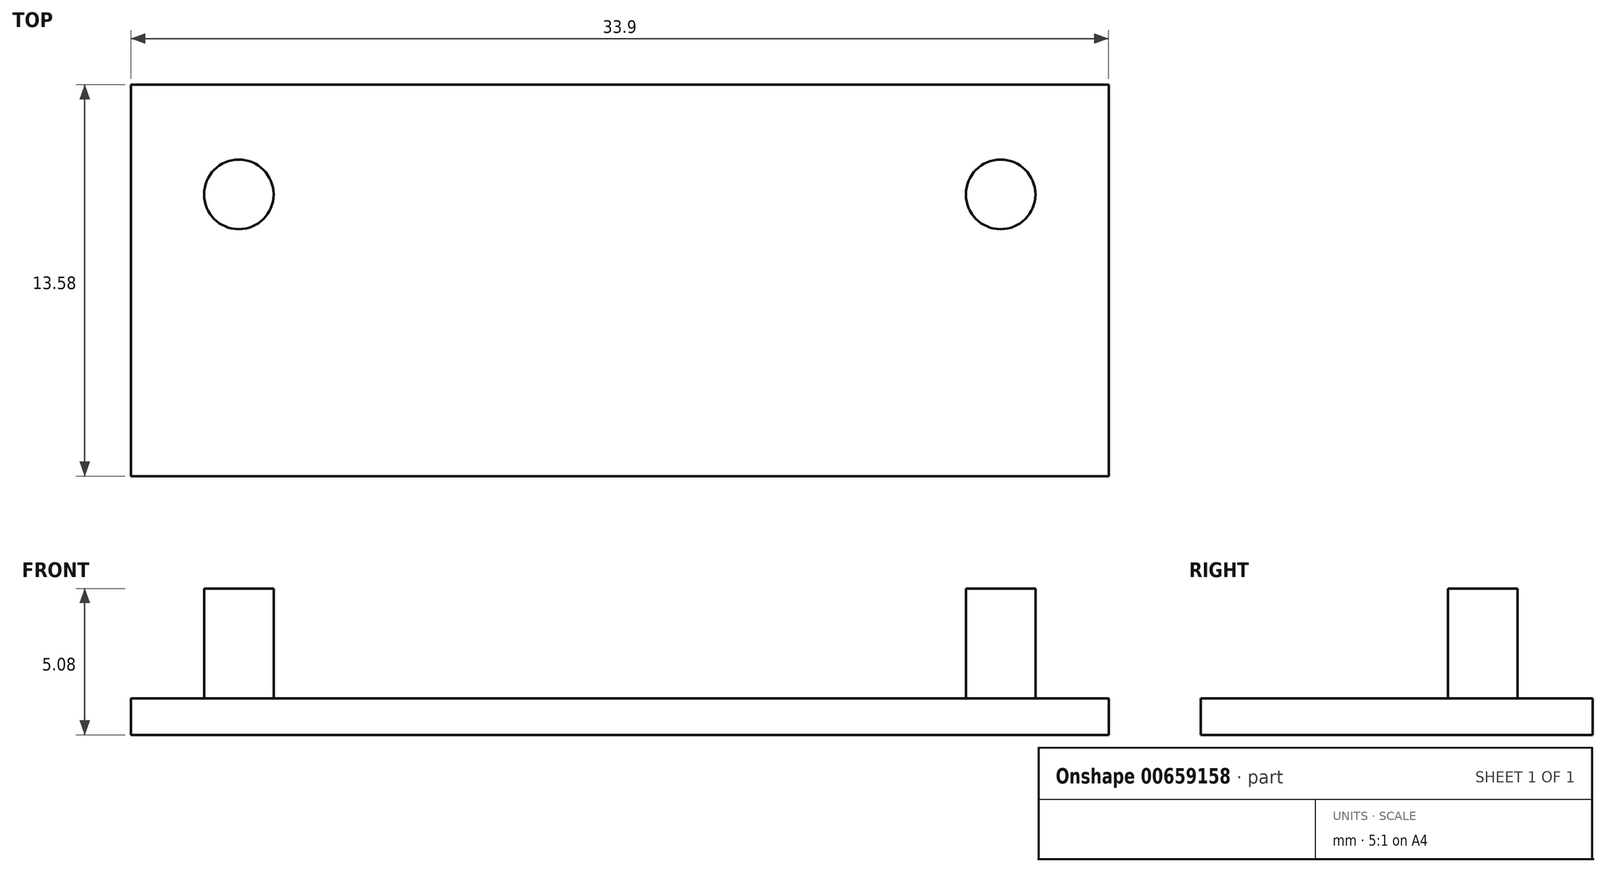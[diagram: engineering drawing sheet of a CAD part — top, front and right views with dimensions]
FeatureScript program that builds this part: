
annotation { "Feature Type Name" : "Feature", "Feature Type Description" : "" }
export const myFeature = defineFeature(function(context is Context, id is Id, definition is map)
    precondition{}
    {
        {
            var Q0;
            Q0=qCreatedBy(makeId("Top.planeOp"),FACE);
            var sketch = newSketch(context, id + "F0", { "sketchPlane" : qUnion([Q0])});
            skLineSegment(sketch, "E0.bottom", {"start": v(16.95, 6.8) * mm, "end": v(-16.95, 6.8) * mm});
            skLineSegment(sketch, "E0.top", {"start": v(16.95, -6.8) * mm, "end": v(-16.95, -6.8) * mm});
            skLineSegment(sketch, "E0.left", {"start": v(16.95, 6.8) * mm, "end": v(16.95, -6.8) * mm});
            skLineSegment(sketch, "E0.right", {"start": v(-16.95, 6.8) * mm, "end": v(-16.95, -6.8) * mm});
            skPoint(sketch, "E0.middle", {"position": v(0, 0) * mm});
            skSolve(sketch);
        }
        {
            var Q0;
            Q0 = qSketchRegion(id + "F0", true);
            extrude(context, id + "F1", {"entities" : qUnion([Q0]), "depth" : 1.27 * mm, "offsetDistance" : 25.4 * mm});
        }
        {
            var Q0;
            Q0=makeQuery(id+"F1.opExtrude","CAP_FACE",FACE,{"disambiguationData":[OSD([sQuery(id+"F0.wireOp",EDGE,"E0.bottom"),sQuery(id+"F0.wireOp",EDGE,"E0.top"),sQuery(id+"F0.wireOp",EDGE,"E0.left"),sQuery(id+"F0.wireOp",EDGE,"E0.right")])],"isStart":false});
            var sketch = newSketch(context, id + "F2", { "sketchPlane" : qUnion([Q0])});
            skCircle(sketch, "E1", {"center": v(-13.2, 2.98) * mm, "radius": 1.2 * mm});
            skCircle(sketch, "E2.MirrorC", {"center": v(13.2, 2.98) * mm, "radius": 1.2 * mm});
            skSolve(sketch);
        }
        {
            var Q0;
            Q0 = qSketchRegion(id + "F2", true);
            extrude(context, id + "F3", {"entities" : qUnion([Q0]), "operationType" : NewBodyOperationType.ADD, "depth" : 3.8 * mm, "offsetDistance" : 25.4 * mm});
        }
    });
